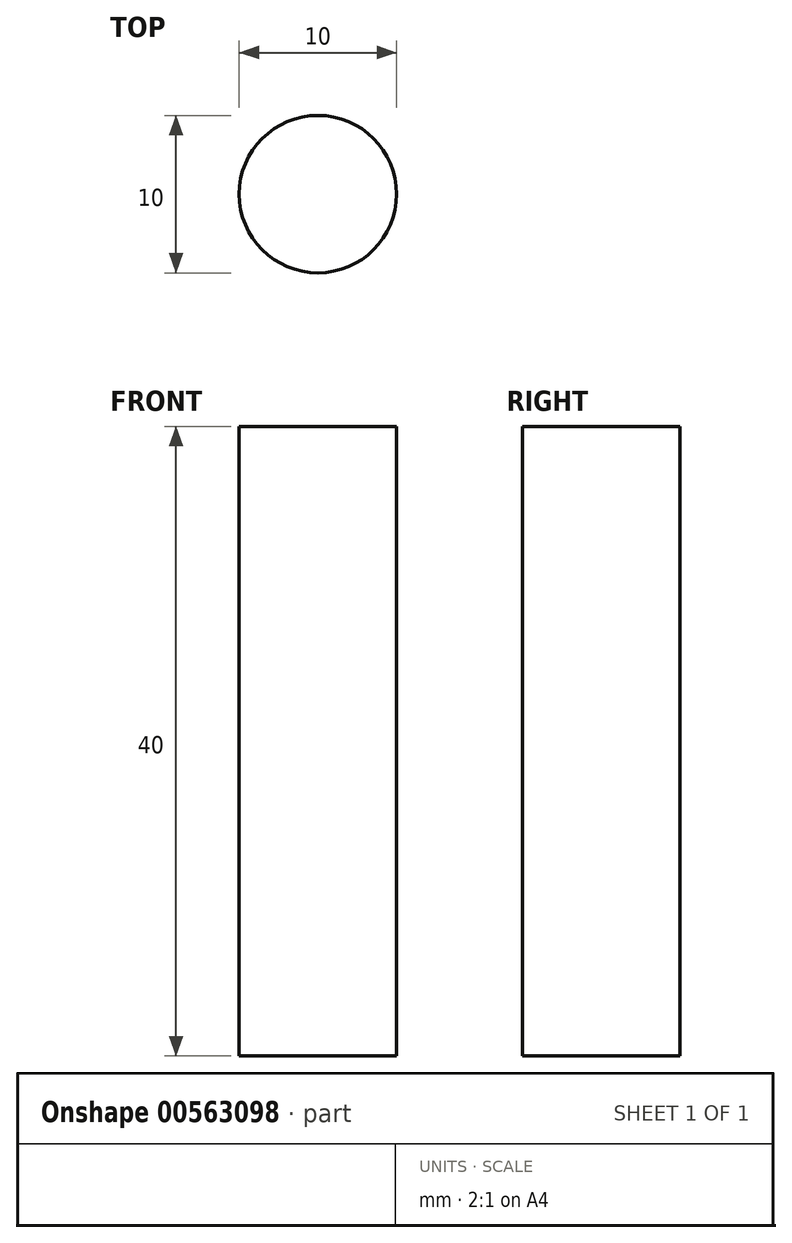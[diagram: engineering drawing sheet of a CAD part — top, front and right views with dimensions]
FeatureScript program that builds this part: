
annotation { "Feature Type Name" : "Feature", "Feature Type Description" : "" }
export const myFeature = defineFeature(function(context is Context, id is Id, definition is map)
    precondition{}
    {
        {
            var Q0;
            Q0=qCreatedBy(makeId("Top.planeOp"),FACE);
            var sketch = newSketch(context, id + "F0", { "sketchPlane" : qUnion([Q0])});
            skCircle(sketch, "E0", {"center": v(0, 0) * mm, "radius": 5 * mm});
            skSolve(sketch);
        }
        {
            var Q0;
            Q0 = qSketchRegion(id + "F0", true);
            extrude(context, id + "F1", {"entities" : qUnion([Q0]), "depth" : 40 * mm, "offsetDistance" : 25 * mm});
        }
    });
